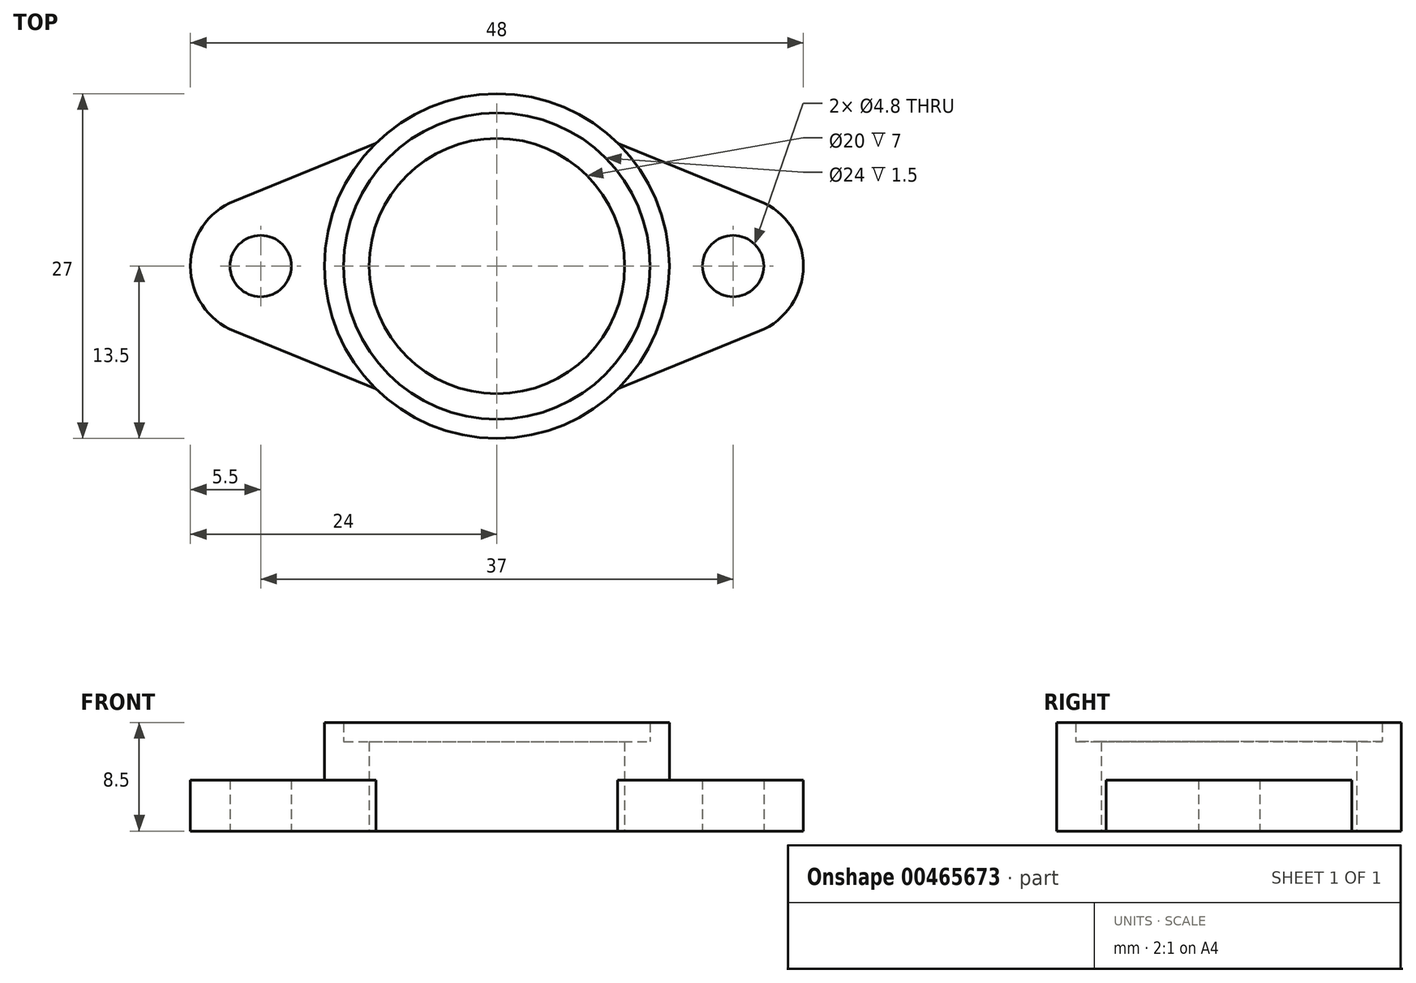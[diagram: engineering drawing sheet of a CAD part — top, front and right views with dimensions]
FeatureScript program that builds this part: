
annotation { "Feature Type Name" : "Feature", "Feature Type Description" : "" }
export const myFeature = defineFeature(function(context is Context, id is Id, definition is map)
    precondition{}
    {
        {
            assignVariable(context, id + "F0", {"name" : "A1", "anyValue" : 4});
        }
        {
            var Q0;
            Q0=qCreatedBy(makeId("Top.planeOp"),FACE);
            var sketch = newSketch(context, id + "F1", { "sketchPlane" : qUnion([Q0])});
            skCircle(sketch, "E0", {"center": v(0, 0) * mm, "radius": 10 * mm});
            skArc(sketch, "E1", {"start": v(-9.47, -9.63) * mm, "mid": v(0, -13.5) * mm, "end": v(9.47, -9.63) * mm});
            skArc(sketch, "E2", {"start": v(-20.58, 5.1) * mm, "mid": v(-24, 0) * mm, "end": v(-20.58, -5.1) * mm});
            skCircle(sketch, "E3", {"center": v(-18.5, 0) * mm, "radius": 2.4 * mm});
            skLineSegment(sketch, "E4", {"start": v(-20.58, 5.1) * mm, "end": v(-9.47, 9.63) * mm});
            skLineSegment(sketch, "E5", {"start": v(-20.58, -5.1) * mm, "end": v(-9.47, -9.63) * mm});
            skArc(sketch, "E6.MirrorC", {"start": v(20.58, 5.1) * mm, "mid": v(24, 0) * mm, "end": v(20.58, -5.1) * mm});
            skCircle(sketch, "E7.MirrorC", {"center": v(18.5, 0) * mm, "radius": 2.4 * mm});
            skLineSegment(sketch, "E8.MirrorCS", {"start": v(20.58, 5.1) * mm, "end": v(9.47, 9.63) * mm});
            skLineSegment(sketch, "E9.MirrorCS", {"start": v(20.58, -5.1) * mm, "end": v(9.47, -9.63) * mm});
            skArc(sketch, "E10.trimOffspring", {"start": v(9.47, 9.63) * mm, "mid": v(0, 13.5) * mm, "end": v(-9.47, 9.63) * mm});
            skSolve(sketch);
        }
        {
            var Q0;
            Q0=makeQuery(id+"F1.imprint","IMPRINT",FACE,{"disambiguationData":[TD([[makeQuery(id+"F1.imprint","IMPRINT",EDGE,{"derivedFrom":sQuery(id+"F1.wireOp",EDGE,"E0")}),-1.0]])]});
            extrude(context, id + "F2", {"entities" : qUnion([Q0]), "depth" : (getVariable(context, 'A1')) * mm});
        }
        {
            var Q0;
            Q0=qCreatedBy(makeId("Front.planeOp"),FACE);
            var sketch = newSketch(context, id + "F3", { "sketchPlane" : qUnion([Q0])});
            skLineSegment(sketch, "E11", {"start": v(-13.5, 4) * mm, "end": v(-13.5, 8.5) * mm});
            skLineSegment(sketch, "E12", {"start": v(-13.5, 8.5) * mm, "end": v(-12, 8.5) * mm});
            skLineSegment(sketch, "E13", {"start": v(-12, 8.5) * mm, "end": v(-12, 7) * mm});
            skLineSegment(sketch, "E14", {"start": v(-12, 7) * mm, "end": v(-10, 7) * mm});
            skLineSegment(sketch, "E15", {"start": v(-10, 7) * mm, "end": v(-10, 4) * mm});
            skLineSegment(sketch, "E16", {"start": v(-10, 4) * mm, "end": v(-13.5, 4) * mm});
            skLineSegment(sketch, "E17.0", {"start": v(-10, 4) * mm, "end": v(10, 4) * mm, "construction": true});
            skLineSegment(sketch, "E18", {"start": v(0, 0) * mm, "end": v(0, 24.06) * mm, "construction": true});
            skPoint(sketch, "E18.endSnap0", {"position": v(0, 4) * mm});
            skSolve(sketch);
        }
        {
            var Q0;
            Q0=makeQuery(id+"F3.imprint","IMPRINT",FACE,{"disambiguationData":[TD([[makeQuery(id+"F3.imprint","IMPRINT",EDGE,{"derivedFrom":sQuery(id+"F3.wireOp",EDGE,"E11")}),-1.0]])]});
            var Q1;
            Q1=sQuery(id+"F3.wireOp",EDGE,"E18");
            revolve(context, id + "F4", {"operationType" : NewBodyOperationType.ADD, "entities" : qUnion([Q0]), "axis" : qUnion([Q1]), "revolveType" : RevolveType.FULL});
        }
    });
